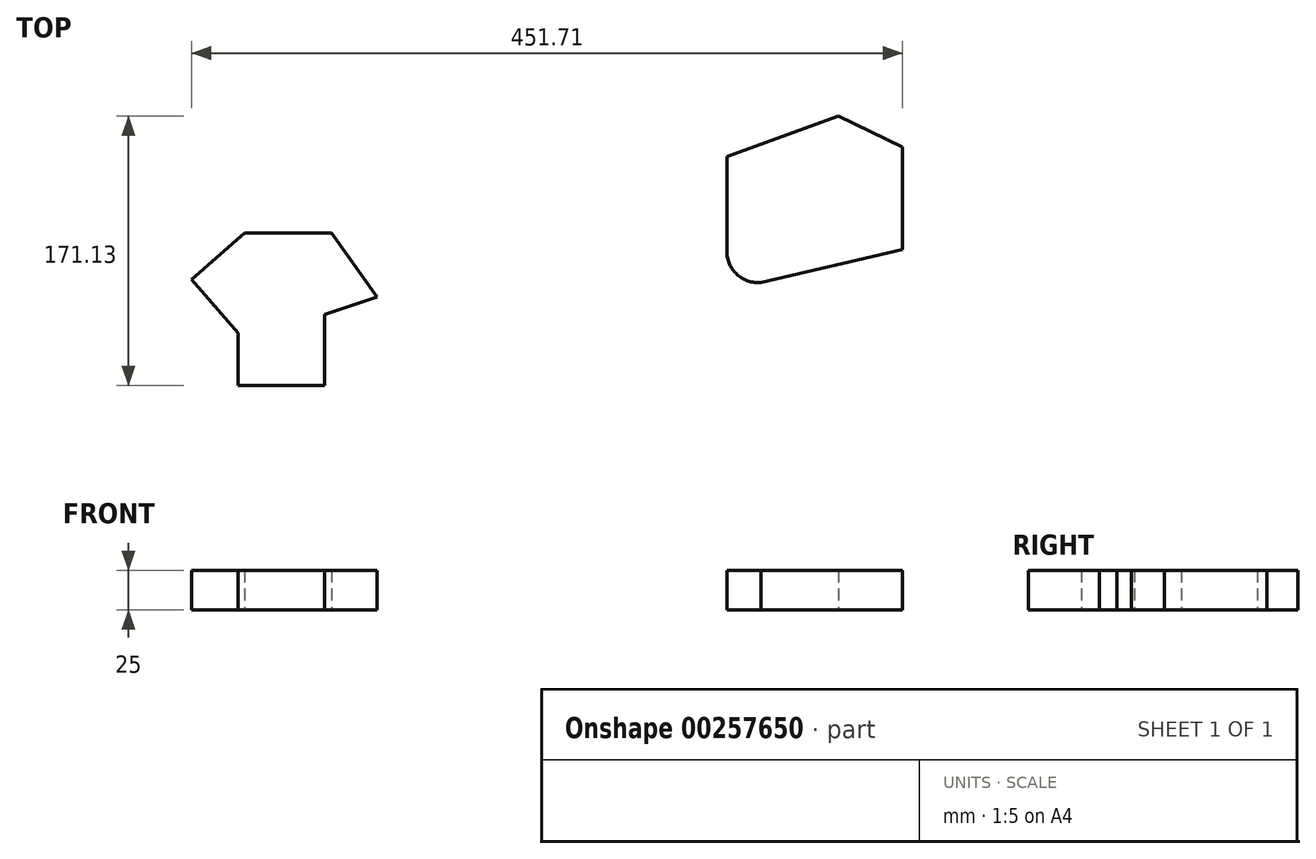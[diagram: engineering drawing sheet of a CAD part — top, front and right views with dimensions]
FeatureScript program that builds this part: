
annotation { "Feature Type Name" : "Feature", "Feature Type Description" : "" }
export const myFeature = defineFeature(function(context is Context, id is Id, definition is map)
    precondition{}
    {
        {
            var Q0;
            Q0=qCreatedBy(makeId("Top.planeOp"),FACE);
            var sketch = newSketch(context, id + "F0", { "sketchPlane" : qUnion([Q0])});
            skLineSegment(sketch, "E0", {"start": v(-103.32, 36.18) * mm, "end": v(-32.38, 62) * mm});
            skLineSegment(sketch, "E1", {"start": v(-32.38, 62) * mm, "end": v(8.36, 42.23) * mm});
            skLineSegment(sketch, "E2", {"start": v(8.36, 42.23) * mm, "end": v(8.36, -22.77) * mm});
            skLineSegment(sketch, "E3", {"start": v(8.36, -22.77) * mm, "end": v(-81.64, -43.75) * mm});
            skLineSegment(sketch, "E4", {"start": v(-103.32, -23.82) * mm, "end": v(-103.32, 36.18) * mm});
            skArc(sketch, "E5", {"start": v(-103.32, -23.82) * mm, "mid": v(-96.86, -38.55) * mm, "end": v(-81.64, -43.75) * mm});
            skLineSegment(sketch, "E6", {"start": v(-413.74, -109.13) * mm, "end": v(-358.74, -109.13) * mm});
            skLineSegment(sketch, "E7", {"start": v(-358.74, -109.13) * mm, "end": v(-358.74, -64.13) * mm});
            skLineSegment(sketch, "E8", {"start": v(-358.74, -64.13) * mm, "end": v(-325.58, -52.95) * mm});
            skLineSegment(sketch, "E9", {"start": v(-325.58, -52.95) * mm, "end": v(-354.47, -12.14) * mm});
            skLineSegment(sketch, "E10", {"start": v(-354.47, -12.14) * mm, "end": v(-409.47, -12.14) * mm});
            skLineSegment(sketch, "E11", {"start": v(-409.47, -12.14) * mm, "end": v(-443.35, -41.75) * mm});
            skLineSegment(sketch, "E12", {"start": v(-443.35, -41.75) * mm, "end": v(-413.74, -75.64) * mm});
            skLineSegment(sketch, "E13", {"start": v(-413.74, -75.64) * mm, "end": v(-413.74, -109.13) * mm});
            skSolve(sketch);
        }
        {
            var Q0;
            Q0=makeQuery(id+"F0.imprint","IMPRINT",FACE,{"disambiguationData":[TD([[makeQuery(id+"F0.imprint","IMPRINT",EDGE,{"derivedFrom":sQuery(id+"F0.wireOp",EDGE,"E6")}),1.0]])]});
            var Q1;
            Q1=makeQuery(id+"F0.imprint","IMPRINT",FACE,{"disambiguationData":[TD([[makeQuery(id+"F0.imprint","IMPRINT",EDGE,{"derivedFrom":sQuery(id+"F0.wireOp",EDGE,"E0")}),-1.0]])]});
            extrude(context, id + "F1", {"entities" : qUnion([Q0, Q1]), "depth" : 25 * mm});
        }
    });
